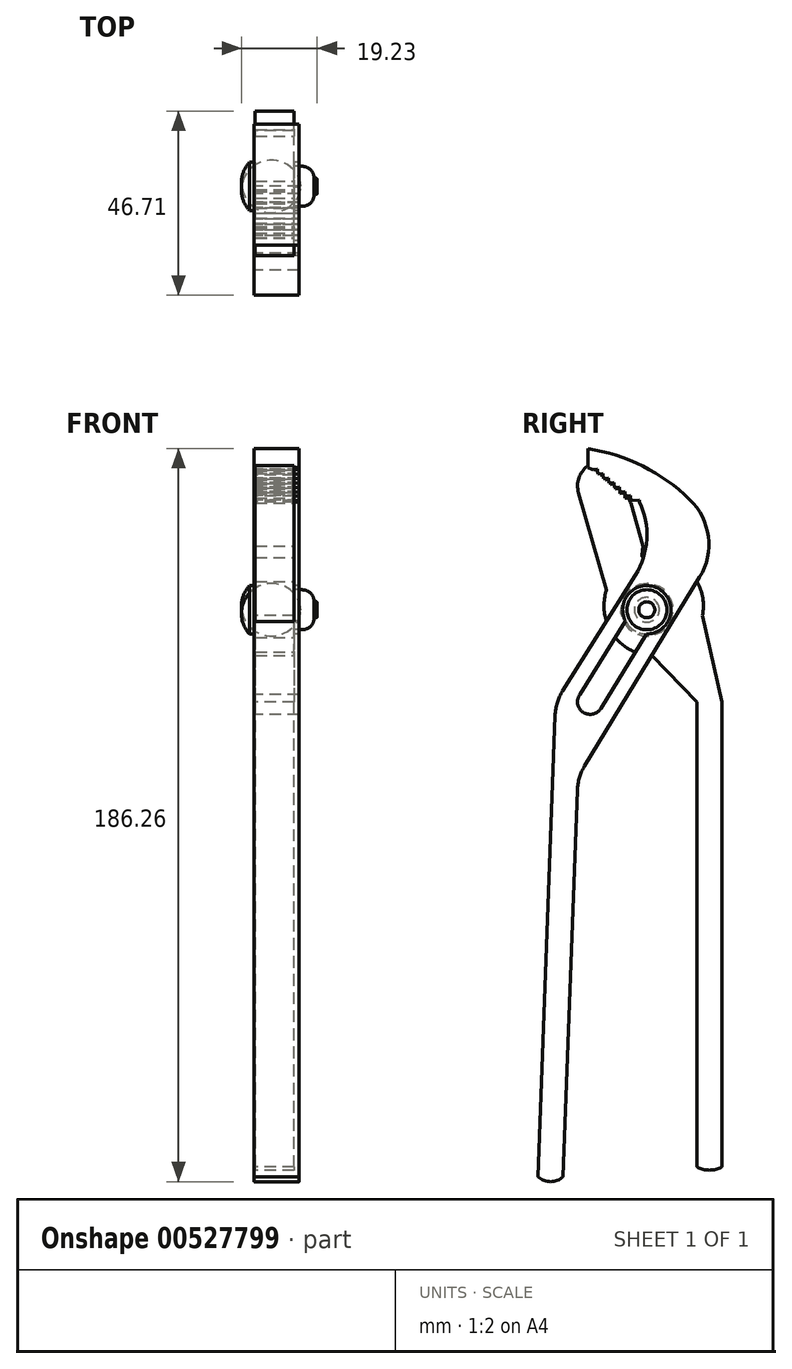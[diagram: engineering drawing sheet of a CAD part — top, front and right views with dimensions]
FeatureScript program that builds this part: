
annotation { "Feature Type Name" : "Feature", "Feature Type Description" : "" }
export const myFeature = defineFeature(function(context is Context, id is Id, definition is map)
    precondition{}
    {
        {
            var Q0;
            Q0=qCreatedBy(makeId("Right.planeOp"),FACE);
            var sketch = newSketch(context, id + "F0", { "sketchPlane" : qUnion([Q0])});
            skLineSegment(sketch, "E0", {"start": v(-0.13, -3.4) * mm, "end": v(-4.44, -120.65) * mm});
            skLineSegment(sketch, "E1", {"start": v(1.8, 2.88) * mm, "end": v(20.25, 32.27) * mm});
            skLineSegment(sketch, "E2", {"start": v(1.91, -120.65) * mm, "end": v(5.53, -22.36) * mm});
            skLineSegment(sketch, "E3", {"start": v(7.37, -16.22) * mm, "end": v(36.6, 31.75) * mm});
            skArc(sketch, "E4", {"start": v(36.6, 31.75) * mm, "mid": v(38.8, 42.08) * mm, "end": v(34.07, 51.51) * mm});
            skArc(sketch, "E5", {"start": v(20.25, 32.27) * mm, "mid": v(23.17, 41.42) * mm, "end": v(21.33, 50.85) * mm});
            skArc(sketch, "E6", {"start": v(34.07, 51.51) * mm, "mid": v(22.14, 59.96) * mm, "end": v(8.23, 64.43) * mm});
            skLineSegment(sketch, "E7", {"start": v(8.23, 64.43) * mm, "end": v(8.23, 59.65) * mm});
            skLineSegment(sketch, "E8", {"start": v(8.23, 59.65) * mm, "end": v(9.39, 59.13) * mm});
            skLineSegment(sketch, "E9", {"start": v(9.39, 59.13) * mm, "end": v(10.64, 59.26) * mm});
            skLineSegment(sketch, "E10", {"start": v(10.64, 59.26) * mm, "end": v(10.77, 58) * mm});
            skLineSegment(sketch, "E11", {"start": v(10.77, 58) * mm, "end": v(12.03, 58.12) * mm});
            skPoint(sketch, "E12.visualSharp", {"position": v(5.65, -19.05) * mm});
            skArc(sketch, "E12.filletArc", {"start": v(7.37, -16.22) * mm, "mid": v(6.06, -19.17) * mm, "end": v(5.53, -22.36) * mm});
            skPoint(sketch, "E13.visualSharp", {"position": v(0, 0) * mm});
            skArc(sketch, "E13.filletArc", {"start": v(1.8, 2.88) * mm, "mid": v(0.43, -0.13) * mm, "end": v(-0.13, -3.4) * mm});
            skLineSegment(sketch, "E14", {"start": v(12.03, 58.12) * mm, "end": v(12.16, 56.85) * mm});
            skLineSegment(sketch, "E15", {"start": v(12.16, 56.85) * mm, "end": v(13.42, 56.98) * mm});
            skLineSegment(sketch, "E16", {"start": v(13.42, 56.98) * mm, "end": v(13.55, 55.72) * mm});
            skLineSegment(sketch, "E17", {"start": v(13.55, 55.72) * mm, "end": v(14.82, 55.85) * mm});
            skLineSegment(sketch, "E18", {"start": v(14.82, 55.85) * mm, "end": v(14.94, 54.59) * mm});
            skLineSegment(sketch, "E19", {"start": v(14.94, 54.59) * mm, "end": v(16.2, 54.71) * mm});
            skLineSegment(sketch, "E20", {"start": v(16.2, 54.71) * mm, "end": v(16.34, 53.44) * mm});
            skLineSegment(sketch, "E21", {"start": v(16.34, 53.44) * mm, "end": v(17.6, 53.56) * mm});
            skLineSegment(sketch, "E22", {"start": v(17.6, 53.56) * mm, "end": v(17.72, 52.3) * mm});
            skLineSegment(sketch, "E23", {"start": v(17.72, 52.3) * mm, "end": v(18.99, 52.44) * mm});
            skLineSegment(sketch, "E24", {"start": v(18.99, 52.44) * mm, "end": v(19.11, 51.17) * mm});
            skLineSegment(sketch, "E25", {"start": v(19.11, 51.17) * mm, "end": v(21.28, 51.38) * mm});
            skLineSegment(sketch, "E26", {"start": v(21.28, 51.38) * mm, "end": v(21.33, 50.85) * mm});
            skPoint(sketch, "E27.orphan", {"position": v(22.99, 45.45) * mm});
            skLineSegment(sketch, "E28", {"start": v(25.78, 21.86) * mm, "end": v(11.5, -1.56) * mm});
            skLineSegment(sketch, "E29", {"start": v(20.59, 25.1) * mm, "end": v(6.16, 1.96) * mm});
            skArc(sketch, "E30", {"start": v(11.5, -1.56) * mm, "mid": v(7.02, -2.57) * mm, "end": v(6.16, 1.96) * mm});
            skLineSegment(sketch, "E31", {"start": v(25.78, 21.86) * mm, "end": v(20.59, 25.1) * mm});
            skCircle(sketch, "E32", {"center": v(23.18, 23.48) * mm, "radius": 6.13 * mm});
            skArc(sketch, "E33", {"start": v(-4.44, -120.65) * mm, "mid": v(-1.26, -121.83) * mm, "end": v(1.91, -120.65) * mm});
            skSolve(sketch);
        }
        {
            var Q0;
            Q0=makeQuery(id+"F0.imprint","IMPRINT",FACE,{"disambiguationData":[TD([[makeQuery(id+"F0.imprint","IMPRINT",EDGE,{"derivedFrom":sQuery(id+"F0.wireOp",EDGE,"E0")}),1.0]])]});
            extrude(context, id + "F1", {"entities" : qUnion([Q0]), "depth" : 11.43 * mm, "offsetDistance" : 25.4 * mm});
        }
        {
            var Q0;
            Q0=qCreatedBy(makeId("Right.planeOp"),FACE);
            var sketch = newSketch(context, id + "F2", { "sketchPlane" : qUnion([Q0])});
            skCircle(sketch, "E34", {"center": v(23.18, 23.48) * mm, "radius": 6.13 * mm});
            skSolve(sketch);
        }
        {
            var Q0;
            Q0=qCreatedBy(makeId("Top.planeOp"),FACE);
            cPlane(context, id + "F3", {"entities" : qUnion([Q0]), "cplaneType" : CPlaneType.OFFSET, "offset" : 23.47 * mm, "width" : 152.4 * mm, "height" : 152.4 * mm});
        }
        {
            var Q0;
            Q0=qCreatedBy(id+"F3.planeOp",FACE);
            var sketch = newSketch(context, id + "F4", { "sketchPlane" : qUnion([Q0])});
            skPoint(sketch, "E35.0", {"position": v(0, 23.18) * mm});
            skLineSegment(sketch, "E36", {"start": v(0, 23.18) * mm, "end": v(-3.17, 23.18) * mm});
            skLineSegment(sketch, "E37", {"start": v(0, 29.32) * mm, "end": v(-1.2, 29.32) * mm});
            skArc(sketch, "E38", {"start": v(-1.2, 29.32) * mm, "mid": v(-2.86, 26.47) * mm, "end": v(-3.18, 23.18) * mm});
            skLineSegment(sketch, "E39", {"start": v(0, 23.18) * mm, "end": v(0, 29.32) * mm});
            skSolve(sketch);
        }
        {
            var Q0;
            Q0 = qSketchRegion(id + "F4", true);
            var Q1;
            Q1=sQuery(id+"F4.wireOp",EDGE,"E36");
            revolve(context, id + "F5", {"operationType" : NewBodyOperationType.ADD, "entities" : qUnion([Q0]), "axis" : qUnion([Q1]), "revolveType" : RevolveType.FULL});
        }
        {
            var Q0;
            Q0=makeQuery(id+"F2.imprint","IMPRINT",FACE,{"disambiguationData":[TD([[makeQuery(id+"F2.imprint","IMPRINT",EDGE,{"derivedFrom":sQuery(id+"F2.wireOp",EDGE,"E34")}),1.0]])]});
            var sketch = newSketch(context, id + "F6", { "sketchPlane" : qUnion([Q0])});
            skCircle(sketch, "E40", {"center": v(23.18, 23.48) * mm, "radius": 3.18 * mm});
            skSolve(sketch);
        }
        {
            var Q0;
            Q0=makeQuery(id+"F6.imprint","IMPRINT",FACE,{"disambiguationData":[TD([[makeQuery(id+"F6.imprint","IMPRINT",EDGE,{"derivedFrom":sQuery(id+"F6.wireOp",EDGE,"E40")}),1.0]])]});
            extrude(context, id + "F7", {"entities" : qUnion([Q0]), "operationType" : NewBodyOperationType.ADD, "depth" : 10.16 * mm, "offsetDistance" : 25.4 * mm});
        }
        {
            var Q0;
            Q0=makeQuery(id+"F7.opExtrude","CAP_FACE",FACE,{"disambiguationData":[OSD([sQuery(id+"F6.wireOp",EDGE,"E40")])],"isStart":false});
            var sketch = newSketch(context, id + "F8", { "sketchPlane" : qUnion([Q0])});
            skArc(sketch, "E41", {"start": v(12.86, 28.18) * mm, "mid": v(33.35, 15) * mm, "end": v(22.5, 36.8) * mm});
            skLineSegment(sketch, "E42", {"start": v(8.7, 60.43) * mm, "end": v(9.85, 59.9) * mm});
            skLineSegment(sketch, "E43", {"start": v(9.85, 59.9) * mm, "end": v(10.11, 58.67) * mm});
            skLineSegment(sketch, "E44", {"start": v(10.11, 58.67) * mm, "end": v(11.36, 58.93) * mm});
            skLineSegment(sketch, "E45", {"start": v(11.36, 58.93) * mm, "end": v(11.36, 57.65) * mm});
            skLineSegment(sketch, "E46", {"start": v(11.36, 57.65) * mm, "end": v(12.63, 57.65) * mm});
            skLineSegment(sketch, "E47", {"start": v(8.7, 60.43) * mm, "end": v(8.12, 59.99) * mm});
            skLineSegment(sketch, "E48", {"start": v(12.63, 57.65) * mm, "end": v(12.63, 56.39) * mm});
            skLineSegment(sketch, "E49", {"start": v(12.63, 56.39) * mm, "end": v(13.9, 56.55) * mm});
            skLineSegment(sketch, "E50", {"start": v(13.9, 56.55) * mm, "end": v(13.9, 55.28) * mm});
            skLineSegment(sketch, "E51", {"start": v(13.9, 55.28) * mm, "end": v(15.15, 55.45) * mm});
            skLineSegment(sketch, "E52", {"start": v(15.15, 55.45) * mm, "end": v(15.15, 54.18) * mm});
            skLineSegment(sketch, "E53", {"start": v(15.15, 54.18) * mm, "end": v(16.41, 54.32) * mm});
            skLineSegment(sketch, "E54", {"start": v(16.41, 54.32) * mm, "end": v(16.41, 53.04) * mm});
            skLineSegment(sketch, "E55", {"start": v(16.41, 53.04) * mm, "end": v(17.67, 53.18) * mm});
            skLineSegment(sketch, "E56", {"start": v(17.67, 53.18) * mm, "end": v(17.67, 51.9) * mm});
            skLineSegment(sketch, "E57", {"start": v(17.67, 51.9) * mm, "end": v(18.94, 51.9) * mm});
            skLineSegment(sketch, "E58", {"start": v(5.84, 53.18) * mm, "end": v(12.87, 28.47) * mm});
            skPoint(sketch, "E59.visualSharp", {"position": v(4.65, 57.36) * mm});
            skArc(sketch, "E59.filletArc", {"start": v(8.12, 59.99) * mm, "mid": v(5.92, 56.94) * mm, "end": v(5.84, 53.18) * mm});
            skArc(sketch, "E60", {"start": v(18.94, 51.9) * mm, "mid": v(18.83, 51.18) * mm, "end": v(19.2, 50.54) * mm});
            skLineSegment(sketch, "E61", {"start": v(22.2, 39.6) * mm, "end": v(21.89, 37.38) * mm});
            skPoint(sketch, "E62.visualSharp", {"position": v(21.79, 36.65) * mm});
            skArc(sketch, "E62.filletArc", {"start": v(21.89, 37.38) * mm, "mid": v(22.04, 36.94) * mm, "end": v(22.5, 36.8) * mm});
            skPoint(sketch, "E63.visualSharp", {"position": v(12.9, 28.32) * mm});
            skArc(sketch, "E63.filletArc", {"start": v(12.86, 28.18) * mm, "mid": v(12.89, 28.32) * mm, "end": v(12.87, 28.47) * mm});
            skLineSegment(sketch, "E64", {"start": v(19.2, 50.54) * mm, "end": v(8.56, 43.62) * mm});
            skLineSegment(sketch, "E65", {"start": v(19.2, 50.54) * mm, "end": v(22.2, 39.6) * mm});
            skSolve(sketch);
        }
        {
            var Q0;
            Q0=makeQuery(id+"F8.imprint","IMPRINT",FACE,{"disambiguationData":[TD([[makeQuery(id+"F8.imprint","IMPRINT",EDGE,{"derivedFrom":sQuery(id+"F8.wireOp",EDGE,"E42")}),-1.0]])]});
            var Q1;
            Q1=makeQuery(id+"F8.imprint","IMPRINT",FACE,{"disambiguationData":[TD([[makeQuery(id+"F8.imprint","IMPRINT",EDGE,{"derivedFrom":sQuery(id+"F8.wireOp",EDGE,"E41")}),1.0]])]});
            extrude(context, id + "F9", {"entities" : qUnion([Q0, Q1]), "operationType" : NewBodyOperationType.ADD, "oppositeDirection" : true, "depth" : 9.9 * mm, "offsetDistance" : 25.4 * mm});
        }
        {
            var Q0;
            {var subQ0=sQuery(id+"F8.wireOp",EDGE,"E41");Q0=makeQuery(id+"F9.boolean.opBoolean","SPLIT",FACE,{"disambiguationData":[TD([makeQuery(id+"F1.opExtrude","SWEPT_FACE",FACE,{"disambiguationData":[OSD([sQuery(id+"F0.wireOp",EDGE,"E3")])]})])],"derivedFrom":makeQuery(id+"F9.opExtrude","CAP_FACE",FACE,{"disambiguationData":[OSD([sQuery(id+"F6.wireOp",EDGE,"E40"),subQ0,sQuery(id+"F8.wireOp",EDGE,"E42"),sQuery(id+"F8.wireOp",EDGE,"E43"),sQuery(id+"F8.wireOp",EDGE,"E44"),sQuery(id+"F8.wireOp",EDGE,"E45"),sQuery(id+"F8.wireOp",EDGE,"E46"),sQuery(id+"F8.wireOp",EDGE,"E47"),sQuery(id+"F8.wireOp",EDGE,"E48"),sQuery(id+"F8.wireOp",EDGE,"E49"),sQuery(id+"F8.wireOp",EDGE,"E50"),sQuery(id+"F8.wireOp",EDGE,"E51"),sQuery(id+"F8.wireOp",EDGE,"E52"),sQuery(id+"F8.wireOp",EDGE,"E53"),sQuery(id+"F8.wireOp",EDGE,"E54"),sQuery(id+"F8.wireOp",EDGE,"E55"),sQuery(id+"F8.wireOp",EDGE,"E56"),sQuery(id+"F8.wireOp",EDGE,"E57"),sQuery(id+"F8.wireOp",EDGE,"E58"),sQuery(id+"F8.wireOp",EDGE,"E59.filletArc"),sQuery(id+"F8.wireOp",EDGE,"E60"),sQuery(id+"F8.wireOp",EDGE,"7t0B5DLs-AQbe-sONx-7pQD-v0wmRc2Mh898"),sQuery(id+"F8.wireOp",EDGE,"K9TN5Zlx-7xN4-ySNA-y2cH-JalfzJvUBM8R"),sQuery(id+"F8.wireOp",EDGE,"AIVCIhSe-ViQb-UifZ-tNyf-mhJj6x05lkRF"),sQuery(id+"F8.wireOp",EDGE,"E61"),sQuery(id+"F8.wireOp",EDGE,"E62.filletArc"),sQuery(id+"F8.wireOp",EDGE,"E63.filletArc")])],"isStart":false})});}
            var sketch = newSketch(context, id + "F10", { "sketchPlane" : qUnion([Q0])});
            skLineSegment(sketch, "E66", {"start": v(-37.32, 22.01) * mm, "end": v(-42.27, 0) * mm});
            skLineSegment(sketch, "E67", {"start": v(-42.27, 0) * mm, "end": v(-42.27, -118.1) * mm});
            skLineSegment(sketch, "E68", {"start": v(-35.92, -118.1) * mm, "end": v(-35.92, 0) * mm});
            skLineSegment(sketch, "E69", {"start": v(-24.44, 11.8) * mm, "end": v(-35.92, 0) * mm});
            skArc(sketch, "E70", {"start": v(-42.27, -118.1) * mm, "mid": v(-39.1, -118.9) * mm, "end": v(-35.92, -118.1) * mm});
            skSolve(sketch);
        }
        {
            var Q0;
            {var subQ0=sQuery(id+"F10.wireOp",EDGE,"E66");Q0=makeQuery(id+"F10.imprint","IMPRINT",FACE,{"disambiguationData":[TD([[makeQuery(id+"F10.imprint","IMPRINT",EDGE,{"derivedFrom":subQ0}),1.0]])]});}
            extrude(context, id + "F11", {"entities" : qUnion([Q0]), "operationType" : NewBodyOperationType.ADD, "oppositeDirection" : true, "depth" : 9.9 * mm, "offsetDistance" : 25.4 * mm});
        }
        {
            var Q0;
            {var subQ0=sQuery(id+"F6.wireOp",EDGE,"E40");Q0=makeQuery(id+"F9.boolean.opBoolean","MERGE",FACE,{"derivedFrom":[makeQuery(id+"F7.opExtrude","CAP_FACE",FACE,{"disambiguationData":[OSD([subQ0])],"isStart":false}),makeQuery(id+"F9.opExtrude","CAP_FACE",FACE,{"disambiguationData":[OSD([subQ0,sQuery(id+"F8.wireOp",EDGE,"E41"),sQuery(id+"F8.wireOp",EDGE,"E42"),sQuery(id+"F8.wireOp",EDGE,"E43"),sQuery(id+"F8.wireOp",EDGE,"E44"),sQuery(id+"F8.wireOp",EDGE,"E45"),sQuery(id+"F8.wireOp",EDGE,"E46"),sQuery(id+"F8.wireOp",EDGE,"E47"),sQuery(id+"F8.wireOp",EDGE,"E48"),sQuery(id+"F8.wireOp",EDGE,"E49"),sQuery(id+"F8.wireOp",EDGE,"E50"),sQuery(id+"F8.wireOp",EDGE,"E51"),sQuery(id+"F8.wireOp",EDGE,"E52"),sQuery(id+"F8.wireOp",EDGE,"E53"),sQuery(id+"F8.wireOp",EDGE,"E54"),sQuery(id+"F8.wireOp",EDGE,"E55"),sQuery(id+"F8.wireOp",EDGE,"E56"),sQuery(id+"F8.wireOp",EDGE,"E57"),sQuery(id+"F8.wireOp",EDGE,"E58"),sQuery(id+"F8.wireOp",EDGE,"E59.filletArc"),sQuery(id+"F8.wireOp",EDGE,"E60"),sQuery(id+"F8.wireOp",EDGE,"E61"),sQuery(id+"F8.wireOp",EDGE,"E62.filletArc"),sQuery(id+"F8.wireOp",EDGE,"E63.filletArc"),sQuery(id+"F8.wireOp",EDGE,"E65")])],"isStart":true})]});}
            var sketch = newSketch(context, id + "F12", { "sketchPlane" : qUnion([Q0])});
            skCircle(sketch, "E71", {"center": v(23.18, 23.48) * mm, "radius": 5.08 * mm});
            skSolve(sketch);
        }
        {
            var Q0;
            Q0 = qSketchRegion(id + "F12", true);
            extrude(context, id + "F13", {"entities" : qUnion([Q0]), "operationType" : NewBodyOperationType.ADD, "depth" : 5.08 * mm, "offsetDistance" : 25.4 * mm});
        }
        {
            var Q0;
            Q0=makeQuery(id+"F13.opExtrude","CAP_FACE",FACE,{"disambiguationData":[OSD([sQuery(id+"F12.wireOp",EDGE,"E71")])],"isStart":false});
            fillet(context, id + "F14", {"entities" : qUnion([Q0]), "radius" : 3.05 * mm, "tangentPropagation" : true, "allowEdgeOverflow" : false});
        }
        {
            var Q0;
            Q0=makeQuery(id+"F13.opExtrude","CAP_FACE",FACE,{"disambiguationData":[OSD([sQuery(id+"F12.wireOp",EDGE,"E71")])],"isStart":false});
            extrude(context, id + "F15", {"entities" : qUnion([Q0]), "operationType" : NewBodyOperationType.ADD, "depth" : 0.76 * mm, "offsetDistance" : 25.4 * mm});
        }
        {
            var Q0;
            Q0=makeQuery(id+"F15.opExtrude","CAP_FACE",FACE,{"disambiguationData":[OSD([sQuery(id+"F12.wireOp",EDGE,"E71")])],"isStart":false});
            fillet(context, id + "F16", {"entities" : qUnion([Q0]), "radius" : 0.25 * mm, "tangentPropagation" : true, "allowEdgeOverflow" : false});
        }
    });
